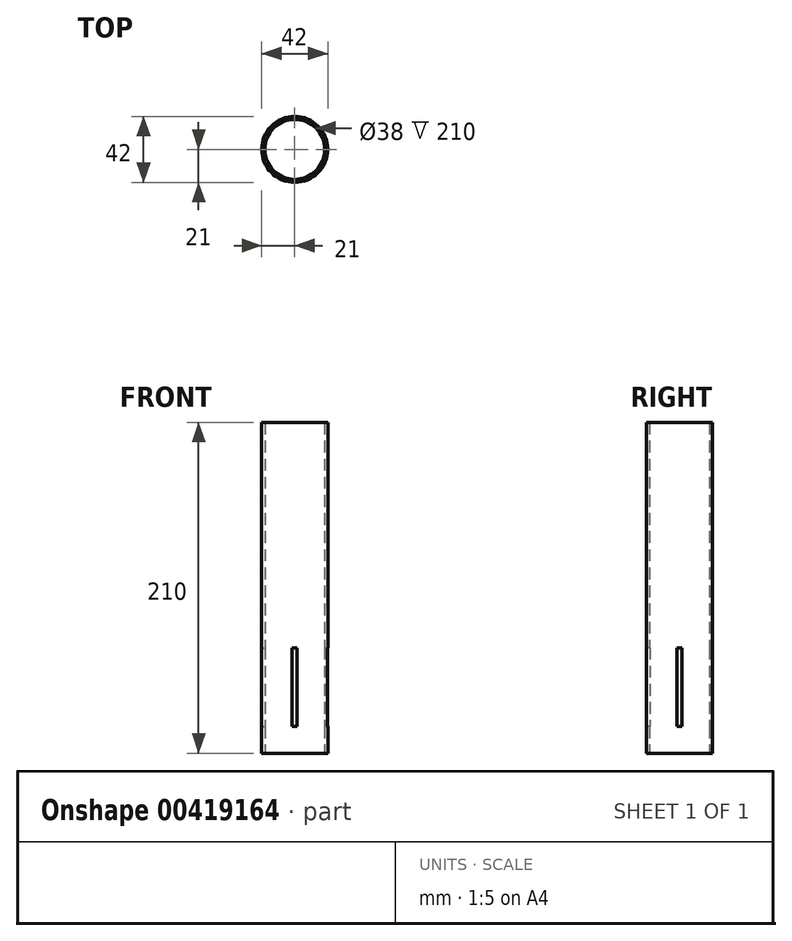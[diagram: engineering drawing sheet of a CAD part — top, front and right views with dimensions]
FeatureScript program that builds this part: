
annotation { "Feature Type Name" : "Feature", "Feature Type Description" : "" }
export const myFeature = defineFeature(function(context is Context, id is Id, definition is map)
    precondition{}
    {
        {
            var Q0;
            Q0=qCreatedBy(makeId("Top.planeOp"),FACE);
            var sketch = newSketch(context, id + "F0", { "sketchPlane" : qUnion([Q0])});
            skCircle(sketch, "E0", {"center": v(0, 0) * mm, "radius": 19 * mm});
            skCircle(sketch, "E1", {"center": v(0, 0) * mm, "radius": 21 * mm});
            skSolve(sketch);
        }
        {
            var Q0;
            Q0 = qSketchRegion(id + "F0", true);
            extrude(context, id + "F1", {"entities" : qUnion([Q0]), "depth" : 210 * mm});
        }
        {
            var Q0;
            Q0=qCreatedBy(makeId("Front.planeOp"),FACE);
            var sketch = newSketch(context, id + "F2", { "sketchPlane" : qUnion([Q0])});
            skLineSegment(sketch, "E2", {"start": v(0, 0) * mm, "end": v(0, 17) * mm});
            skLineSegment(sketch, "E3", {"start": v(-1.59, 17) * mm, "end": v(1.59, 17) * mm});
            skLineSegment(sketch, "E4", {"start": v(-1.59, 17) * mm, "end": v(-1.59, 67) * mm});
            skLineSegment(sketch, "E5", {"start": v(-1.59, 67) * mm, "end": v(1.59, 67) * mm});
            skLineSegment(sketch, "E6", {"start": v(1.59, 67) * mm, "end": v(1.59, 17) * mm});
            skSolve(sketch);
        }
        {
            var Q0;
            Q0 = qSketchRegion(id + "F2", true);
            extrude(context, id + "F3", {"entities" : qUnion([Q0]), "operationType" : NewBodyOperationType.REMOVE, "endBound" : BoundingType.SYMMETRIC, "oppositeDirection" : true, "depth" : 1000 * mm});
        }
        {
            var Q0;
            Q0=qCreatedBy(makeId("Right.planeOp"),FACE);
            var sketch = newSketch(context, id + "F4", { "sketchPlane" : qUnion([Q0])});
            skLineSegment(sketch, "E7", {"start": v(0, 0) * mm, "end": v(0, 17) * mm});
            skLineSegment(sketch, "E8", {"start": v(1.59, 17) * mm, "end": v(-1.59, 17) * mm});
            skPoint(sketch, "E9.endSnap0", {"position": v(0, 17) * mm});
            skPoint(sketch, "E9.end.orphan", {"position": v(0, 78.7) * mm});
            skPoint(sketch, "E9.start.orphan", {"position": v(0, 17) * mm});
            skLineSegment(sketch, "E10", {"start": v(1.59, 17) * mm, "end": v(1.59, 67) * mm});
            skLineSegment(sketch, "E11", {"start": v(1.59, 67) * mm, "end": v(-1.59, 67) * mm});
            skLineSegment(sketch, "E12", {"start": v(-1.59, 67) * mm, "end": v(-1.59, 17) * mm});
            skSolve(sketch);
        }
        {
            var Q0;
            Q0 = qSketchRegion(id + "F4", true);
            extrude(context, id + "F5", {"entities" : qUnion([Q0]), "operationType" : NewBodyOperationType.REMOVE, "endBound" : BoundingType.SYMMETRIC, "oppositeDirection" : true, "depth" : 1000 * mm});
        }
    });
